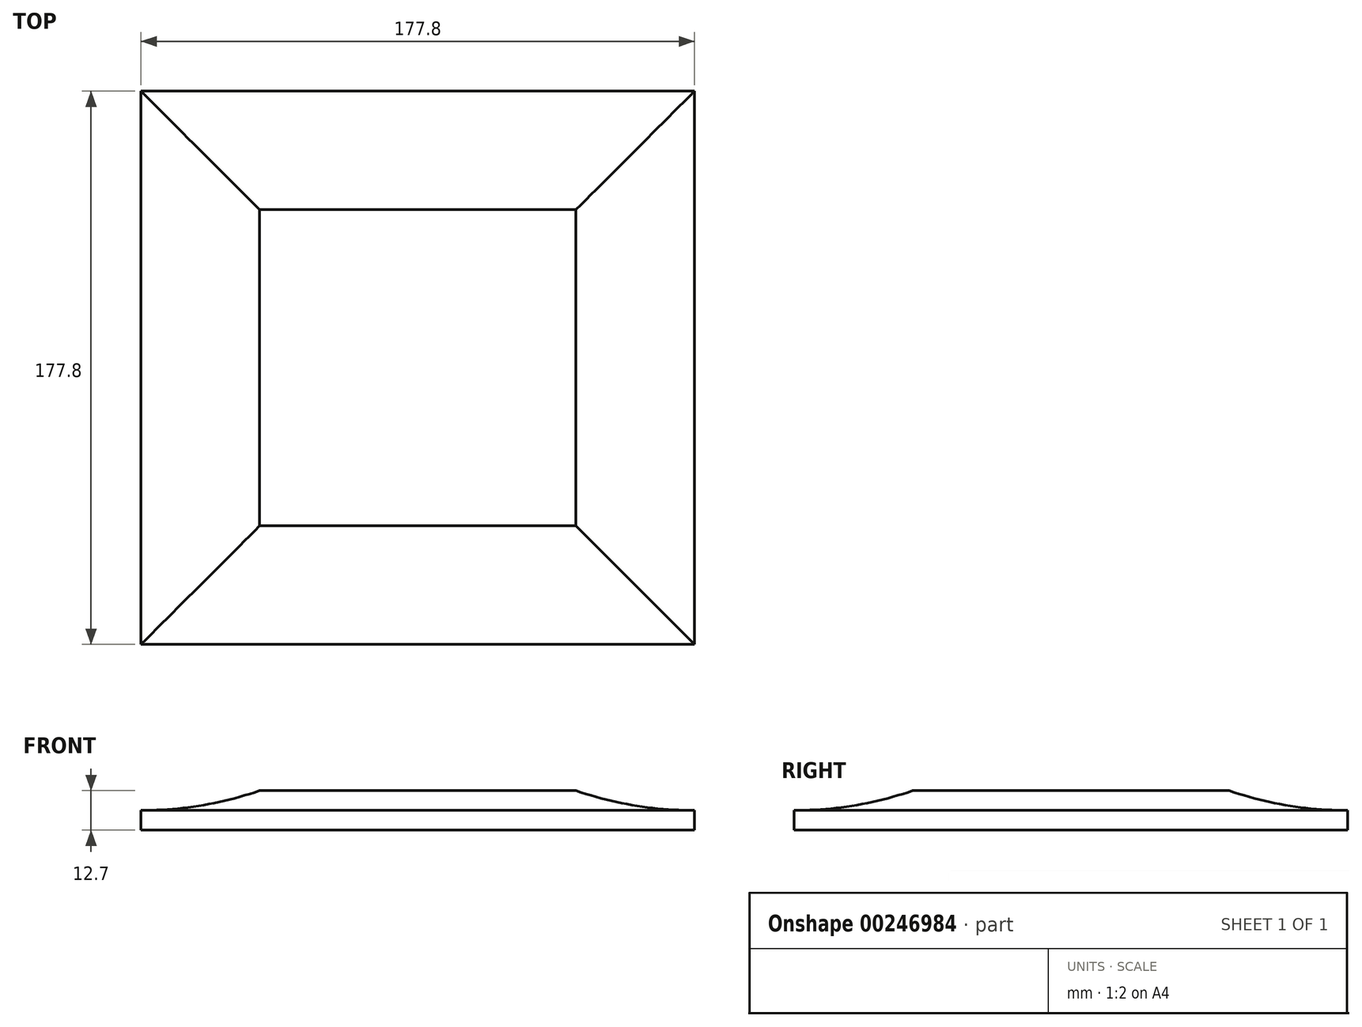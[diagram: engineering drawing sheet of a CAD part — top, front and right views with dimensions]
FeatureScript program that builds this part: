
annotation { "Feature Type Name" : "Feature", "Feature Type Description" : "" }
export const myFeature = defineFeature(function(context is Context, id is Id, definition is map)
    precondition{}
    {
        {
            var Q0;
            Q0=qCreatedBy(makeId("Top.planeOp"),FACE);
            var sketch = newSketch(context, id + "F0", { "sketchPlane" : qUnion([Q0])});
            skLineSegment(sketch, "E0.bottom", {"start": v(88.9, -88.9) * mm, "end": v(-88.9, -88.9) * mm});
            skLineSegment(sketch, "E0.top", {"start": v(88.9, 88.9) * mm, "end": v(-88.9, 88.9) * mm});
            skLineSegment(sketch, "E0.left", {"start": v(88.9, -88.9) * mm, "end": v(88.9, 88.9) * mm});
            skLineSegment(sketch, "E0.right", {"start": v(-88.9, -88.9) * mm, "end": v(-88.9, 88.9) * mm});
            skPoint(sketch, "E0.middle", {"position": v(0, 0) * mm});
            skSolve(sketch);
        }
        {
            var Q0;
            Q0=qCreatedBy(makeId("Front.planeOp"),FACE);
            var sketch = newSketch(context, id + "F1", { "sketchPlane" : qUnion([Q0])});
            skPoint(sketch, "E1.0", {"position": v(88.9, 0) * mm});
            skLineSegment(sketch, "E2", {"start": v(0, 0) * mm, "end": v(88.9, 0) * mm});
            skLineSegment(sketch, "E3", {"start": v(88.9, 0) * mm, "end": v(88.9, 6.35) * mm});
            skLineSegment(sketch, "E4", {"start": v(88.9, 6.35) * mm, "end": v(99.58, 6.35) * mm, "construction": true});
            skLineSegment(sketch, "E5", {"start": v(0, 0) * mm, "end": v(0, 12.7) * mm});
            skLineSegment(sketch, "E6", {"start": v(0, 12.7) * mm, "end": v(50.8, 12.7) * mm});
            skArc(sketch, "E7", {"start": v(88.9, 6.35) * mm, "mid": v(69.59, 7.95) * mm, "end": v(50.8, 12.7) * mm});
            skSolve(sketch);
        }
        {
            var Q0;
            Q0=makeQuery(id+"F1.imprint","IMPRINT",FACE,{"disambiguationData":[TD([[makeQuery(id+"F1.imprint","IMPRINT",EDGE,{"derivedFrom":sQuery(id+"F1.wireOp",EDGE,"E2")}),1.0]])]});
            var Q1;
            Q1=sQuery(id+"F0.wireOp",EDGE,"E0.left");
            var Q2;
            Q2=sQuery(id+"F0.wireOp",EDGE,"E0.top");
            var Q3;
            Q3=sQuery(id+"F0.wireOp",EDGE,"E0.right");
            var Q4;
            Q4=sQuery(id+"F0.wireOp",EDGE,"E0.bottom");
            sweep(context, id + "F2", {"profiles" : qUnion([Q0]), "path" : qUnion([Q1, Q2, Q3, Q4])});
        }
    });
